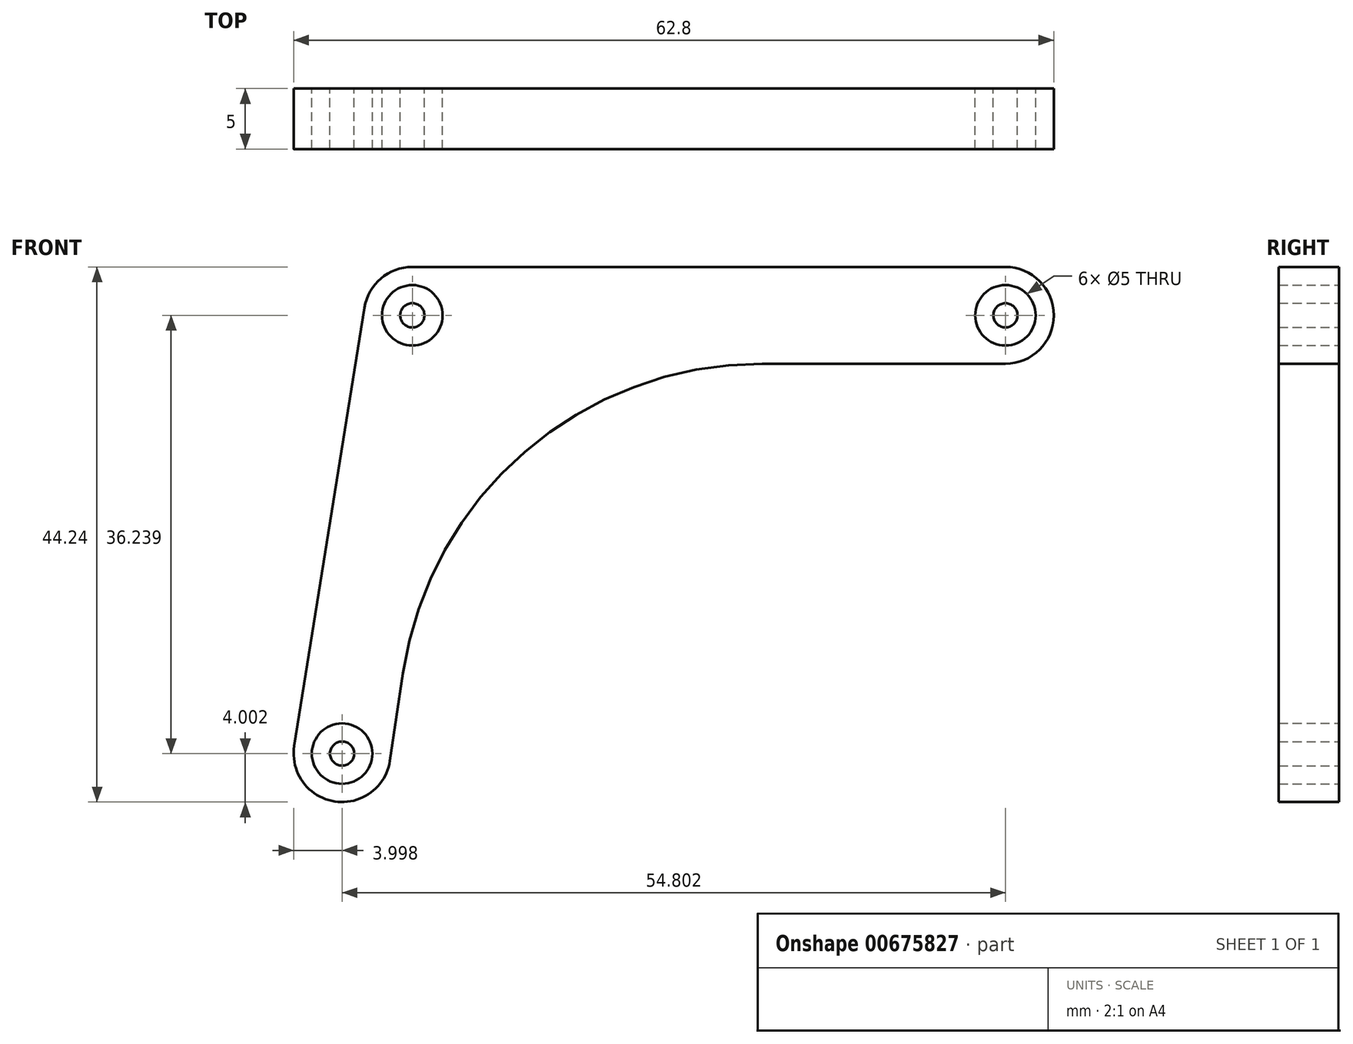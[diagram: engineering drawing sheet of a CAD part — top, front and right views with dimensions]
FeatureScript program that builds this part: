
annotation { "Feature Type Name" : "Feature", "Feature Type Description" : "" }
export const myFeature = defineFeature(function(context is Context, id is Id, definition is map)
    precondition{}
    {
        {
            var Q0;
            Q0=qCreatedBy(makeId("Front.planeOp"),FACE);
            var sketch = newSketch(context, id + "F0", { "sketchPlane" : qUnion([Q0])});
            skArc(sketch, "E0", {"start": v(0, 4) * mm, "mid": v(-2.6, 3.04) * mm, "end": v(-3.95, 0.63) * mm});
            skArc(sketch, "E1", {"start": v(49, -4) * mm, "mid": v(53, 0) * mm, "end": v(49, 4) * mm});
            skArc(sketch, "E2", {"start": v(-9.75, -35.6) * mm, "mid": v(-6.41, -40.2) * mm, "end": v(-1.85, -36.82) * mm});
            skLineSegment(sketch, "E3", {"start": v(-3.95, 0.63) * mm, "end": v(-9.75, -35.6) * mm});
            skLineSegment(sketch, "E4", {"start": v(0, 4) * mm, "end": v(49, 4) * mm});
            skLineSegment(sketch, "E5", {"start": v(-1.85, -36.82) * mm, "end": v(-0.78, -29.6) * mm});
            skLineSegment(sketch, "E6", {"start": v(49, -4) * mm, "end": v(28.9, -4) * mm});
            skArc(sketch, "E7.filletArc", {"start": v(28.9, -4) * mm, "mid": v(9.3, -11.29) * mm, "end": v(-0.78, -29.6) * mm});
            skCircle(sketch, "E8", {"center": v(0, 0) * mm, "radius": 2.5 * mm});
            skCircle(sketch, "E9", {"center": v(0, 0) * mm, "radius": 1 * mm});
            skCircle(sketch, "E10", {"center": v(49, 0) * mm, "radius": 1 * mm});
            skCircle(sketch, "E11", {"center": v(49, 0) * mm, "radius": 2.5 * mm});
            skCircle(sketch, "E12", {"center": v(-5.8, -36.24) * mm, "radius": 2.5 * mm});
            skCircle(sketch, "E13", {"center": v(-5.8, -36.24) * mm, "radius": 1 * mm});
            skSolve(sketch);
        }
        {
            var Q0;
            Q0=makeQuery(id+"F0.imprint","IMPRINT",FACE,{"disambiguationData":[TD([[makeQuery(id+"F0.imprint","IMPRINT",EDGE,{"derivedFrom":sQuery(id+"F0.wireOp",EDGE,"E0")}),1.0]])]});
            var Q1;
            Q1=makeQuery(id+"F0.imprint","IMPRINT",FACE,{"disambiguationData":[TD([[makeQuery(id+"F0.imprint","IMPRINT",EDGE,{"derivedFrom":sQuery(id+"F0.wireOp",EDGE,"E10")}),1.0]])]});
            var Q2;
            Q2=makeQuery(id+"F0.imprint","IMPRINT",FACE,{"disambiguationData":[TD([[makeQuery(id+"F0.imprint","IMPRINT",EDGE,{"derivedFrom":sQuery(id+"F0.wireOp",EDGE,"E9")}),1.0]])]});
            var Q3;
            Q3=makeQuery(id+"F0.imprint","IMPRINT",FACE,{"disambiguationData":[TD([[makeQuery(id+"F0.imprint","IMPRINT",EDGE,{"derivedFrom":sQuery(id+"F0.wireOp",EDGE,"E13")}),1.0]])]});
            extrude(context, id + "F1", {"entities" : qUnion([Q0, Q1, Q2, Q3]), "endBound" : BoundingType.SYMMETRIC, "depth" : 5 * mm, "offsetDistance" : 25 * mm});
        }
    });
